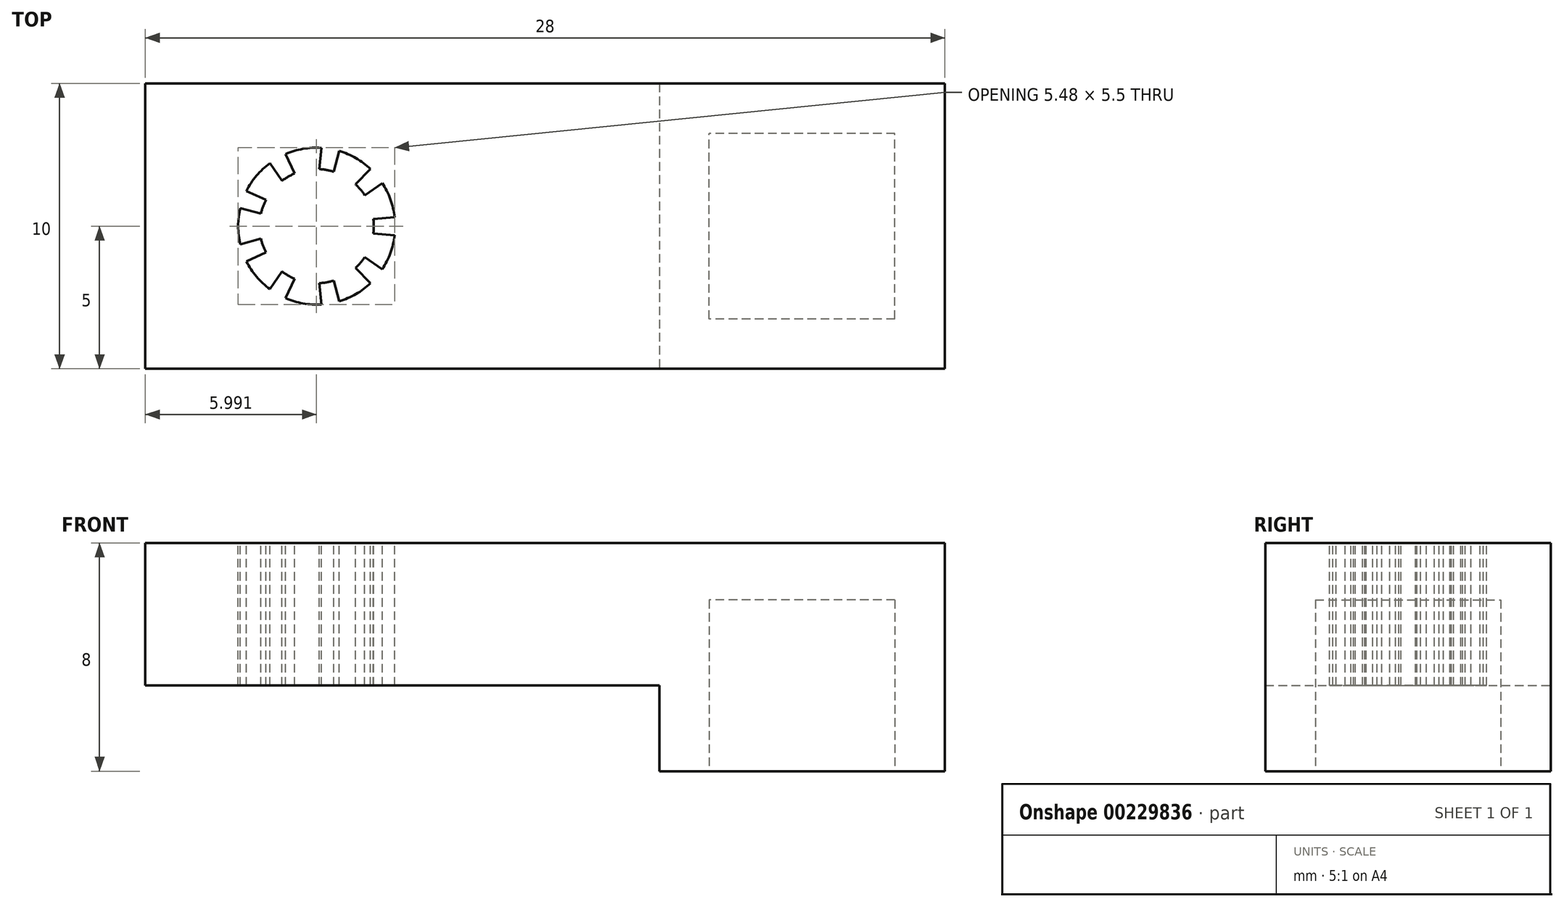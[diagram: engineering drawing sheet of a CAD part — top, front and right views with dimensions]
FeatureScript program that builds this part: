
annotation { "Feature Type Name" : "Feature", "Feature Type Description" : "" }
export const myFeature = defineFeature(function(context is Context, id is Id, definition is map)
    precondition{}
    {
        {
            var Q0;
            Q0=qCreatedBy(makeId("Top.planeOp"),FACE);
            var sketch = newSketch(context, id + "F0", { "sketchPlane" : qUnion([Q0])});
            skLineSegment(sketch, "E0.bottom", {"start": v(0, -5) * mm, "end": v(28, -5) * mm});
            skLineSegment(sketch, "E0.top", {"start": v(0, 5) * mm, "end": v(28, 5) * mm});
            skLineSegment(sketch, "E0.left", {"start": v(0, -5) * mm, "end": v(0, 5) * mm});
            skLineSegment(sketch, "E0.right", {"start": v(28, -5) * mm, "end": v(28, 5) * mm});
            skSolve(sketch);
        }
        {
            var Q0;
            Q0 = qSketchRegion(id + "F0", true);
            extrude(context, id + "F1", {"entities" : qUnion([Q0]), "depth" : 5 * mm});
        }
        {
            var Q0;
            Q0=makeQuery(id+"F1.opExtrude","CAP_FACE",FACE,{"disambiguationData":[OSD([sQuery(id+"F0.wireOp",EDGE,"E0.bottom"),sQuery(id+"F0.wireOp",EDGE,"E0.top"),sQuery(id+"F0.wireOp",EDGE,"E0.left"),sQuery(id+"F0.wireOp",EDGE,"E0.right")])],"isStart":false});
            var sketch = newSketch(context, id + "F2", { "sketchPlane" : qUnion([Q0])});
            skArc(sketch, "E1", {"start": v(8.73, 0.32) * mm, "mid": v(8.58, 0.94) * mm, "end": v(8.3, 1.51) * mm});
            skCircle(sketch, "E2", {"center": v(6, 0) * mm, "radius": 2 * mm});
            skLineSegment(sketch, "E3", {"start": v(8.73, -0.32) * mm, "end": v(7.98, -0.25) * mm});
            skLineSegment(sketch, "E4", {"start": v(7.98, -0.25) * mm, "end": v(7.98, 0.25) * mm});
            skLineSegment(sketch, "E5", {"start": v(7.98, 0.25) * mm, "end": v(8.73, 0.32) * mm});
            skLineSegment(sketch, "E6.1.0", {"start": v(7.36, 1.47) * mm, "end": v(7.89, 2) * mm});
            skLineSegment(sketch, "E6.1.1", {"start": v(7.68, 1.08) * mm, "end": v(7.36, 1.47) * mm});
            skLineSegment(sketch, "E6.1.2", {"start": v(8.3, 1.51) * mm, "end": v(7.68, 1.08) * mm});
            skLineSegment(sketch, "E6.2.0", {"start": v(6.1, 2) * mm, "end": v(6.16, 2.75) * mm});
            skLineSegment(sketch, "E6.2.1", {"start": v(6.6, 1.9) * mm, "end": v(6.1, 2) * mm});
            skLineSegment(sketch, "E6.2.2", {"start": v(6.79, 2.63) * mm, "end": v(6.6, 1.9) * mm});
            skLineSegment(sketch, "E6.3.0", {"start": v(4.79, 1.6) * mm, "end": v(4.36, 2.2) * mm});
            skLineSegment(sketch, "E6.3.1", {"start": v(5.23, 1.85) * mm, "end": v(4.79, 1.6) * mm});
            skLineSegment(sketch, "E6.3.2", {"start": v(4.9, 2.52) * mm, "end": v(5.23, 1.85) * mm});
            skLineSegment(sketch, "E6.4.0", {"start": v(4.05, 0.44) * mm, "end": v(3.32, 0.64) * mm});
            skLineSegment(sketch, "E6.4.1", {"start": v(4.22, 0.92) * mm, "end": v(4.05, 0.44) * mm});
            skLineSegment(sketch, "E6.4.2", {"start": v(3.54, 1.23) * mm, "end": v(4.22, 0.92) * mm});
            skLineSegment(sketch, "E6.5.0", {"start": v(4.22, -0.92) * mm, "end": v(3.54, -1.23) * mm});
            skLineSegment(sketch, "E6.5.1", {"start": v(4.05, -0.44) * mm, "end": v(4.22, -0.92) * mm});
            skLineSegment(sketch, "E6.5.2", {"start": v(3.32, -0.64) * mm, "end": v(4.05, -0.44) * mm});
            skLineSegment(sketch, "E6.6.0", {"start": v(5.23, -1.85) * mm, "end": v(4.9, -2.52) * mm});
            skLineSegment(sketch, "E6.6.1", {"start": v(4.79, -1.6) * mm, "end": v(5.23, -1.85) * mm});
            skLineSegment(sketch, "E6.6.2", {"start": v(4.36, -2.2) * mm, "end": v(4.79, -1.6) * mm});
            skLineSegment(sketch, "E6.7.0", {"start": v(6.6, -1.9) * mm, "end": v(6.79, -2.63) * mm});
            skLineSegment(sketch, "E6.7.1", {"start": v(6.1, -2) * mm, "end": v(6.6, -1.9) * mm});
            skLineSegment(sketch, "E6.7.2", {"start": v(6.16, -2.75) * mm, "end": v(6.1, -2) * mm});
            skLineSegment(sketch, "E6.8.0", {"start": v(7.68, -1.08) * mm, "end": v(8.3, -1.51) * mm});
            skLineSegment(sketch, "E6.8.1", {"start": v(7.36, -1.47) * mm, "end": v(7.68, -1.08) * mm});
            skLineSegment(sketch, "E6.8.2", {"start": v(7.89, -2) * mm, "end": v(7.36, -1.47) * mm});
            skArc(sketch, "E7.trimOffspring", {"start": v(7.89, 2) * mm, "mid": v(7.38, 2.38) * mm, "end": v(6.79, 2.63) * mm});
            skArc(sketch, "E8.trimOffspring", {"start": v(6.16, 2.75) * mm, "mid": v(5.52, 2.7) * mm, "end": v(4.9, 2.52) * mm});
            skArc(sketch, "E9.trimOffspring", {"start": v(4.36, 2.2) * mm, "mid": v(3.9, 1.77) * mm, "end": v(3.54, 1.23) * mm});
            skArc(sketch, "E10.trimOffspring", {"start": v(3.32, 0.64) * mm, "mid": v(3.25, 0) * mm, "end": v(3.32, -0.64) * mm});
            skArc(sketch, "E11.trimOffspring", {"start": v(3.54, -1.23) * mm, "mid": v(3.9, -1.77) * mm, "end": v(4.36, -2.2) * mm});
            skArc(sketch, "E12.trimOffspring", {"start": v(4.9, -2.52) * mm, "mid": v(5.52, -2.7) * mm, "end": v(6.16, -2.75) * mm});
            skArc(sketch, "E13.trimOffspring", {"start": v(6.79, -2.63) * mm, "mid": v(7.38, -2.38) * mm, "end": v(7.89, -2) * mm});
            skArc(sketch, "E14.trimOffspring", {"start": v(8.3, -1.51) * mm, "mid": v(8.58, -0.94) * mm, "end": v(8.73, -0.32) * mm});
            skSolve(sketch);
        }
        {
            var Q0;
            Q0 = qSketchRegion(id + "F2", true);
            extrude(context, id + "F3", {"entities" : qUnion([Q0]), "operationType" : NewBodyOperationType.REMOVE, "oppositeDirection" : true, "depth" : 6 * mm});
        }
        {
            var Q0;
            Q0=makeQuery(id+"F1.opExtrude","CAP_FACE",FACE,{"disambiguationData":[OSD([sQuery(id+"F0.wireOp",EDGE,"E0.bottom"),sQuery(id+"F0.wireOp",EDGE,"E0.top"),sQuery(id+"F0.wireOp",EDGE,"E0.left"),sQuery(id+"F0.wireOp",EDGE,"E0.right")])],"isStart":true});
            var sketch = newSketch(context, id + "F4", { "sketchPlane" : qUnion([Q0])});
            skLineSegment(sketch, "E15.bottom", {"start": v(28, -5) * mm, "end": v(18, -5) * mm});
            skLineSegment(sketch, "E15.top", {"start": v(28, 5) * mm, "end": v(18, 5) * mm});
            skLineSegment(sketch, "E15.left", {"start": v(28, -5) * mm, "end": v(28, 5) * mm});
            skLineSegment(sketch, "E15.right", {"start": v(18, -5) * mm, "end": v(18, 5) * mm});
            skSolve(sketch);
        }
        {
            var Q0;
            Q0 = qSketchRegion(id + "F4", true);
            extrude(context, id + "F5", {"entities" : qUnion([Q0]), "operationType" : NewBodyOperationType.ADD, "depth" : 3 * mm});
        }
        {
            var Q0;
            Q0=makeQuery(id+"F5.opExtrude","CAP_FACE",FACE,{"disambiguationData":[OSD([sQuery(id+"F4.wireOp",EDGE,"E15.bottom"),sQuery(id+"F4.wireOp",EDGE,"E15.top"),sQuery(id+"F4.wireOp",EDGE,"E15.left"),sQuery(id+"F4.wireOp",EDGE,"E15.right")])],"isStart":false});
            var sketch = newSketch(context, id + "F6", { "sketchPlane" : qUnion([Q0])});
            skLineSegment(sketch, "E16.bottom", {"start": v(26.25, 3.25) * mm, "end": v(19.75, 3.25) * mm});
            skLineSegment(sketch, "E16.top", {"start": v(26.25, -3.25) * mm, "end": v(19.75, -3.25) * mm});
            skLineSegment(sketch, "E16.left", {"start": v(26.25, 3.25) * mm, "end": v(26.25, -3.25) * mm});
            skLineSegment(sketch, "E16.right", {"start": v(19.75, 3.25) * mm, "end": v(19.75, -3.25) * mm});
            skPoint(sketch, "E16.middle", {"position": v(23, 0) * mm});
            skPoint(sketch, "E16.middle.positionSnap0", {"position": v(23, 5) * mm});
            skPoint(sketch, "E16.middle.positionSnap1", {"position": v(28, 0) * mm});
            skPoint(sketch, "E16.centerSnap0", {"position": v(23, 5) * mm});
            skPoint(sketch, "E16.centerSnap1", {"position": v(28, 0) * mm});
            skSolve(sketch);
        }
        {
            var Q0;
            Q0 = qSketchRegion(id + "F6", true);
            extrude(context, id + "F7", {"entities" : qUnion([Q0]), "operationType" : NewBodyOperationType.REMOVE, "oppositeDirection" : true, "depth" : 6 * mm});
        }
    });
